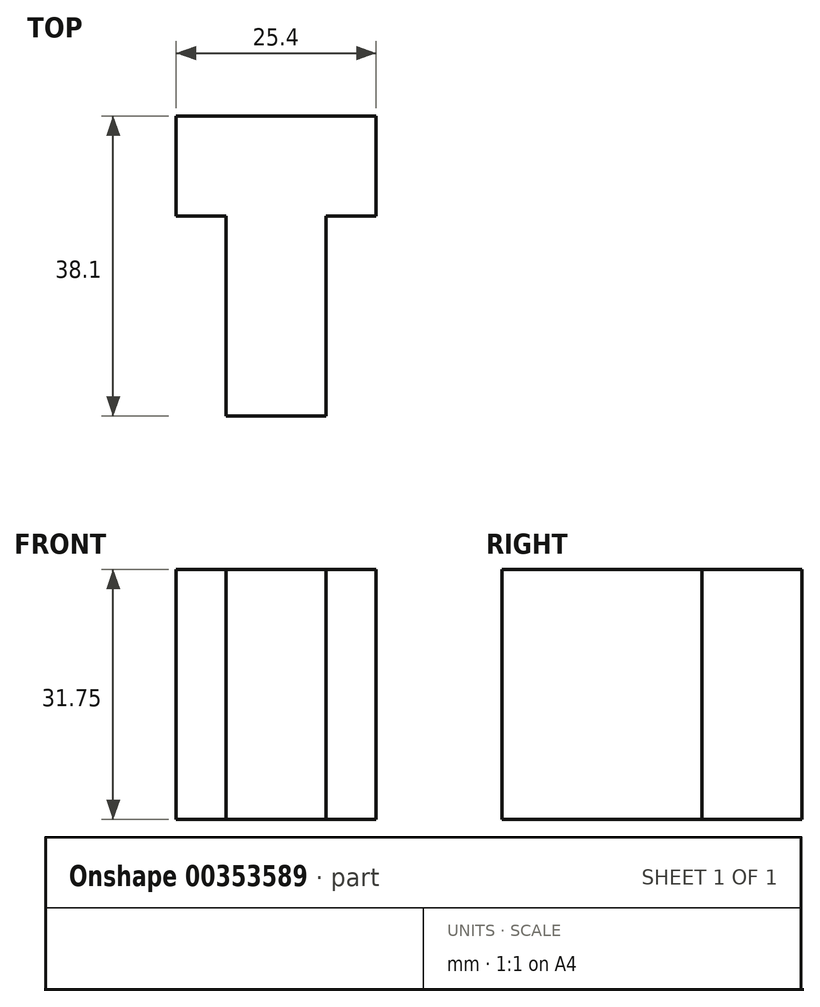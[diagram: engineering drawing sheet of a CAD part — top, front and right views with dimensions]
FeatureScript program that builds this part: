
annotation { "Feature Type Name" : "Feature", "Feature Type Description" : "" }
export const myFeature = defineFeature(function(context is Context, id is Id, definition is map)
    precondition{}
    {
        {
            var Q0;
            Q0=qCreatedBy(makeId("Top.planeOp"),FACE);
            var sketch = newSketch(context, id + "F0", { "sketchPlane" : qUnion([Q0])});
            skLineSegment(sketch, "E0", {"start": v(6.35, 0) * mm, "end": v(6.35, 25.4) * mm});
            skLineSegment(sketch, "E1", {"start": v(6.35, 25.4) * mm, "end": v(0, 25.4) * mm});
            skLineSegment(sketch, "E2", {"start": v(0, 25.4) * mm, "end": v(0, 38.1) * mm});
            skLineSegment(sketch, "E3", {"start": v(0, 38.1) * mm, "end": v(25.4, 38.1) * mm});
            skLineSegment(sketch, "E4", {"start": v(25.4, 38.1) * mm, "end": v(25.4, 25.4) * mm});
            skLineSegment(sketch, "E5", {"start": v(25.4, 25.4) * mm, "end": v(19.05, 25.4) * mm});
            skLineSegment(sketch, "E6", {"start": v(19.05, 25.4) * mm, "end": v(19.05, 0) * mm});
            skLineSegment(sketch, "E7", {"start": v(19.05, 0) * mm, "end": v(6.35, 0) * mm});
            skSolve(sketch);
        }
        {
            var Q0;
            Q0=makeQuery(id+"F0.imprint","IMPRINT",FACE,{"disambiguationData":[TD([[makeQuery(id+"F0.imprint","IMPRINT",EDGE,{"derivedFrom":sQuery(id+"F0.wireOp",EDGE,"E0")}),-1.0]])]});
            extrude(context, id + "F1", {"entities" : qUnion([Q0]), "depth" : 31.75 * mm});
        }
    });
